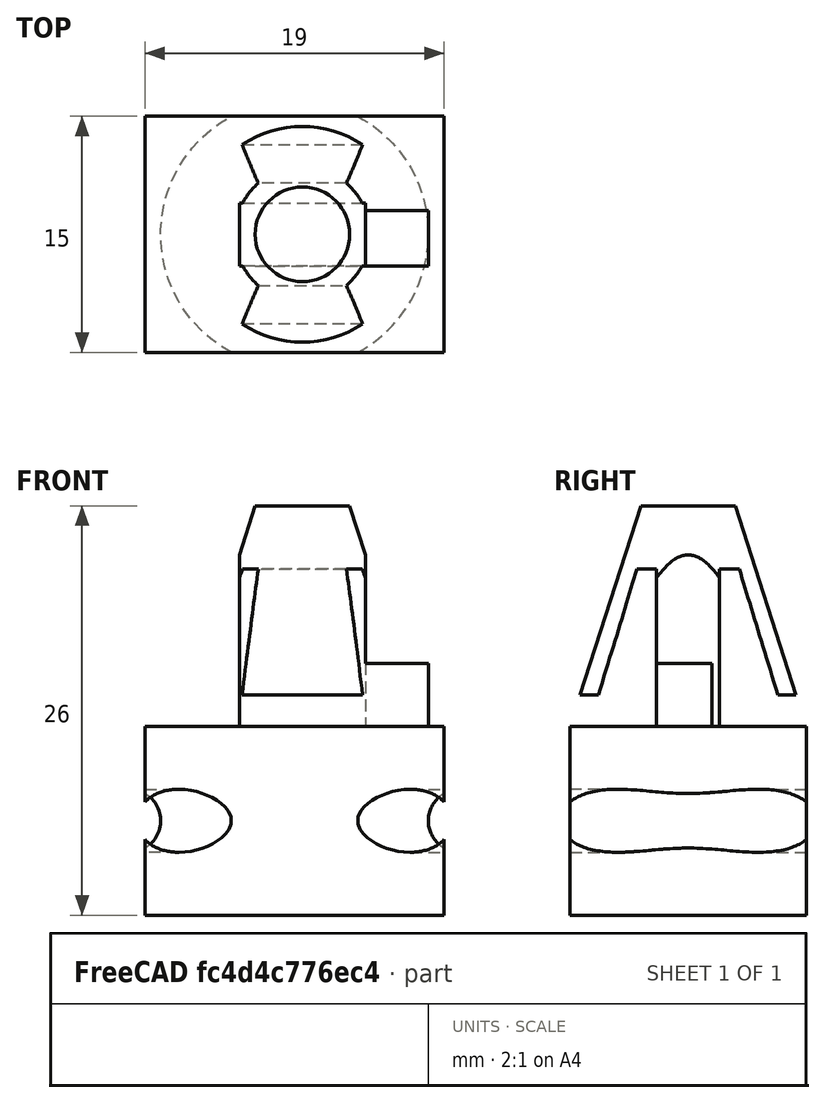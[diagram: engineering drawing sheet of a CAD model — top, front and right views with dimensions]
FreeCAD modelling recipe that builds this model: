
FCSTD DOCUMENT  (FreeCAD 0.14R2935 (Git))
Label: Soporte_maletero_corsa
License: CC-BY 3.0
LicenseURL: http://creativecommons.org/licenses/by/3.0/
objects: Part::Box×10, Part::Cut×9, Part::Cone×1, Part::Torus×1, Part::MultiFuse×1
note: 22 computed .brp shape members not serialized (recipe doc carries the construction recipe); baked Part::Feature solids carry a one-line shape summary decoded from their .brp

FEATURE [Part::Cone] Cone
  Angle = 360
  Height = 14
  Radius1 = 7.5
  Radius2 = 3
FEATURE [Part::Box] Box
  Height = 10
  Length = 20
  Placement = pos=(0,12,0) rot=(0,0,1;0rad)
  Width = 5
FEATURE [Part::Box] Box001
  Height = 18
  Length = 20
  Placement = pos=(0,17.17,-2.83) rot=(1,0,0;0.296705rad)
  Width = 8
FEATURE [Part::Cut] Cut  label="Cuña"
  Base = -> Box
  Placement = pos=(-10,-10,0) rot=(0,0,1;0rad)
  Tool = -> Box001
FEATURE [Part::Box] Box002
  Height = 18
  Length = 20
  Placement = pos=(0,17.17,-2.83) rot=(1,0,0;0.296705rad)
  Width = 8
FEATURE [Part::Box] Box003
  Height = 10
  Length = 20
  Placement = pos=(0,12,0) rot=(0,0,1;0rad)
  Width = 5
FEATURE [Part::Cut] Cut001  label="Cuña001"
  Base = -> Box003
  Placement = pos=(10,10,0) rot=(0,0,1;3.14159rad)
  Tool = -> Box002
FEATURE [Part::Cut] Cut002
  Base = -> Cone
  Tool = -> Cut
FEATURE [Part::Cut] Cut003
  Base = -> Cut002
  Tool = -> Cut001
FEATURE [Part::Box] Box004
  Height = 4
  Length = 11
  Placement = pos=(-3,-2,0) rot=(0,0,1;0rad)
  Width = 3.5
FEATURE [Part::Box] Box005
  Height = 15
  Length = 10
  Placement = pos=(4,-4,0) rot=(0,0,1;0rad)
  Width = 10
FEATURE [Part::Box] Box006
  Height = 15
  Length = 10
  Placement = pos=(-4,-4,0) rot=(0,0,1;1.5708rad)
  Width = 10
FEATURE [Part::Cut] Cut004
  Base = -> Cut003
  Tool = -> Box005
FEATURE [Part::Cut] Cut005
  Base = -> Cut004
  Tool = -> Box006
FEATURE [Part::Box] Box007
  Height = 12
  Length = 19
  Placement = pos=(-10,-7.5,-12) rot=(0,0,1;0rad)
  Width = 15
FEATURE [Part::Box] Box008
  Height = 5
  Length = 10
  Placement = pos=(-5,5,-3) rot=(0,0,1;0rad)
  Width = 10
FEATURE [Part::Box] Box009
  Height = 5
  Length = 10
  Placement = pos=(5,-4,-3) rot=(0,0,1;3.14159rad)
  Width = 10
FEATURE [Part::Cut] Cut006
  Base = -> Cut005
  Tool = -> Box009
FEATURE [Part::Cut] Cut007
  Base = -> Cut006
  Tool = -> Box008
FEATURE [Part::Torus] Torus
  Angle1 = -180
  Angle2 = 180
  Angle3 = 360
  Placement = pos=(-0.5,0,-6) rot=(0,0,1;0rad)
  Radius1 = 10.5
  Radius2 = 2
FEATURE [Part::Cut] Cut008
  Base = -> Box007
  Tool = -> Torus
FEATURE [Part::MultiFuse] Fusion
  Shapes = -> [Box004,Cut007,Cut008]
